# Revit family: 95800 030
name_source: partatom
category: Modelos genéricos
units: mm (PartAtom-declared; Revit-internal decimal feet)

## family parameters
Com base no plano de trabalho = Não
Compartilhado = Não
Corte com vazios quando carregada = Não
Cota do conector redondo = Utilizar diâmetro
Pode hospedar o vergalhão = Não
Ponto de cálculo do ambiente = Não
Sempre na vertical = Sim
Tipo de parte = Normal

## types (1)
- 95800 030
    Acabamento = Scotch Brite
    Descrição = Coifa de parede
    Dimensões = 500 x 900 x 522 a 1002 mm (Altura)
    Elevação padrão = 0 mm  [stored 0 ft]
    Espessura = 1 mm
    Fabricante = Tramontina
    Frequência elétrica = 50 - 60 Hz
    Material predominante = Aço Inox
    Modelo = Coifa Slim Wall 90 Split
    Nível de ruído = 58 dB(A)
    Número de velocidades = 4
    Potência das lâmpadas LED = 2x 1,3 W
    Potência elétrica total = 401 W
    Quantidade de filtros = 3
    Referência do produto = 95800/030
    Segundo material = Vidro bisotado
    Tensão elétrica = 220 V
    Tipo de material = AISI 304
    URL da ficha técnica = https://assets.tramontina.com.br
    URL do fabricante = tramontina.com.br
    URL do produto = https://www.tramontina.com.br
    URL dos arquivos BIM = tramontina.com.br/biblioteca
    Usado em conjunto com = Chaminés complementares
    Vazão = 845 m³/h

note: [stored X ft] marks values corroborated as IEEE doubles in the binary element streams (Revit-internal decimal feet)
